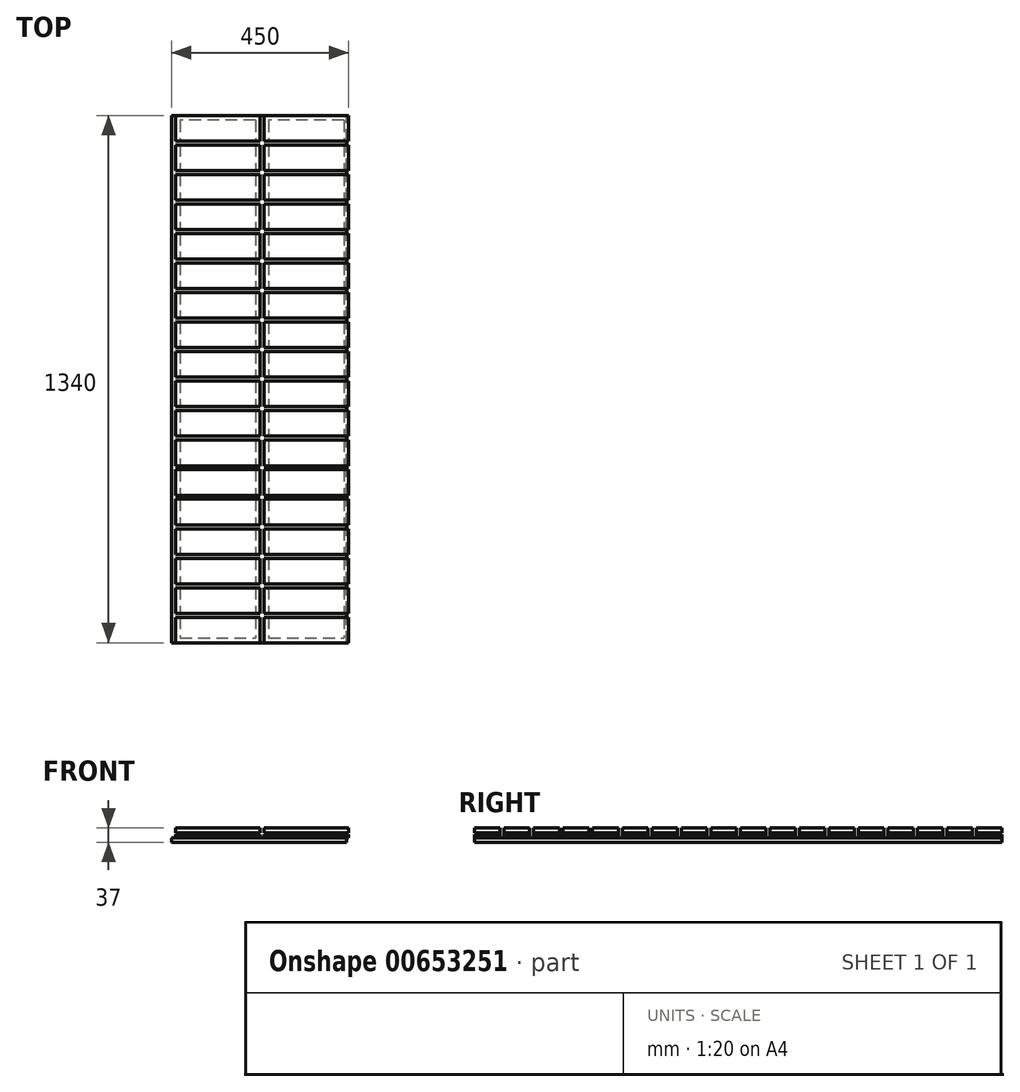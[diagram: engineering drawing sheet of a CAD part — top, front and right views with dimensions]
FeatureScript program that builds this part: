
annotation { "Feature Type Name" : "Feature", "Feature Type Description" : "" }
export const myFeature = defineFeature(function(context is Context, id is Id, definition is map)
    precondition{}
    {
        {
            var Q0;
            Q0=qCreatedBy(makeId("Top.planeOp"),FACE);
            var sketch = newSketch(context, id + "F0", { "sketchPlane" : qUnion([Q0])});
            skLineSegment(sketch, "E0", {"start": v(-211.36, 1125) * mm, "end": v(-211.36, 1190) * mm});
            skLineSegment(sketch, "E1", {"start": v(-211.36, 1190) * mm, "end": v(3.64, 1190) * mm});
            skLineSegment(sketch, "E2", {"start": v(3.64, 1190) * mm, "end": v(3.64, 1125) * mm});
            skLineSegment(sketch, "E3", {"start": v(3.64, 1125) * mm, "end": v(-211.36, 1125) * mm});
            skLineSegment(sketch, "E4", {"start": v(-211.36, 1200) * mm, "end": v(-211.36, 1265) * mm});
            skLineSegment(sketch, "E5", {"start": v(-211.36, 1265) * mm, "end": v(3.64, 1265) * mm});
            skLineSegment(sketch, "E6", {"start": v(3.64, 1265) * mm, "end": v(3.64, 1200) * mm});
            skLineSegment(sketch, "E7", {"start": v(3.64, 1200) * mm, "end": v(-211.36, 1200) * mm});
            skLineSegment(sketch, "E8", {"start": v(-211.36, 1275) * mm, "end": v(-211.36, 1340) * mm});
            skLineSegment(sketch, "E9", {"start": v(-211.36, 1340) * mm, "end": v(3.64, 1340) * mm});
            skLineSegment(sketch, "E10", {"start": v(3.64, 1340) * mm, "end": v(3.64, 1275) * mm});
            skLineSegment(sketch, "E11", {"start": v(3.64, 1275) * mm, "end": v(-211.36, 1275) * mm});
            skLineSegment(sketch, "E12", {"start": v(-436.36, 1125) * mm, "end": v(-436.36, 1190) * mm});
            skLineSegment(sketch, "E13", {"start": v(-436.36, 1190) * mm, "end": v(-221.36, 1190) * mm});
            skLineSegment(sketch, "E14", {"start": v(-221.36, 1190) * mm, "end": v(-221.36, 1125) * mm});
            skLineSegment(sketch, "E15", {"start": v(-221.36, 1125) * mm, "end": v(-436.36, 1125) * mm});
            skLineSegment(sketch, "E16", {"start": v(-436.36, 1200) * mm, "end": v(-436.36, 1265) * mm});
            skLineSegment(sketch, "E17", {"start": v(-436.36, 1265) * mm, "end": v(-221.36, 1265) * mm});
            skLineSegment(sketch, "E18", {"start": v(-221.36, 1265) * mm, "end": v(-221.36, 1200) * mm});
            skLineSegment(sketch, "E19", {"start": v(-221.36, 1200) * mm, "end": v(-436.36, 1200) * mm});
            skLineSegment(sketch, "E20", {"start": v(-436.36, 1275) * mm, "end": v(-436.36, 1340) * mm});
            skLineSegment(sketch, "E21", {"start": v(-436.36, 1340) * mm, "end": v(-221.36, 1340) * mm});
            skLineSegment(sketch, "E22", {"start": v(-221.36, 1340) * mm, "end": v(-221.36, 1275) * mm});
            skLineSegment(sketch, "E23", {"start": v(-221.36, 1275) * mm, "end": v(-436.36, 1275) * mm});
            skLineSegment(sketch, "E24", {"start": v(-211.36, 900) * mm, "end": v(-211.36, 965) * mm});
            skLineSegment(sketch, "E25", {"start": v(-211.36, 965) * mm, "end": v(3.64, 965) * mm});
            skLineSegment(sketch, "E26", {"start": v(3.64, 965) * mm, "end": v(3.64, 900) * mm});
            skLineSegment(sketch, "E27", {"start": v(3.64, 900) * mm, "end": v(-211.36, 900) * mm});
            skLineSegment(sketch, "E28", {"start": v(-211.36, 975) * mm, "end": v(-211.36, 1040) * mm});
            skLineSegment(sketch, "E29", {"start": v(-211.36, 1040) * mm, "end": v(3.64, 1040) * mm});
            skLineSegment(sketch, "E30", {"start": v(3.64, 1040) * mm, "end": v(3.64, 975) * mm});
            skLineSegment(sketch, "E31", {"start": v(3.64, 975) * mm, "end": v(-211.36, 975) * mm});
            skLineSegment(sketch, "E32", {"start": v(-211.36, 1050) * mm, "end": v(-211.36, 1115) * mm});
            skLineSegment(sketch, "E33", {"start": v(-211.36, 1115) * mm, "end": v(3.64, 1115) * mm});
            skLineSegment(sketch, "E34", {"start": v(3.64, 1115) * mm, "end": v(3.64, 1050) * mm});
            skLineSegment(sketch, "E35", {"start": v(3.64, 1050) * mm, "end": v(-211.36, 1050) * mm});
            skLineSegment(sketch, "E36", {"start": v(-436.36, 900) * mm, "end": v(-436.36, 965) * mm});
            skLineSegment(sketch, "E37", {"start": v(-436.36, 965) * mm, "end": v(-221.36, 965) * mm});
            skLineSegment(sketch, "E38", {"start": v(-221.36, 965) * mm, "end": v(-221.36, 900) * mm});
            skLineSegment(sketch, "E39", {"start": v(-221.36, 900) * mm, "end": v(-436.36, 900) * mm});
            skLineSegment(sketch, "E40", {"start": v(-436.36, 975) * mm, "end": v(-436.36, 1040) * mm});
            skLineSegment(sketch, "E41", {"start": v(-436.36, 1040) * mm, "end": v(-221.36, 1040) * mm});
            skLineSegment(sketch, "E42", {"start": v(-221.36, 1040) * mm, "end": v(-221.36, 975) * mm});
            skLineSegment(sketch, "E43", {"start": v(-221.36, 975) * mm, "end": v(-436.36, 975) * mm});
            skLineSegment(sketch, "E44", {"start": v(-436.36, 1050) * mm, "end": v(-436.36, 1115) * mm});
            skLineSegment(sketch, "E45", {"start": v(-436.36, 1115) * mm, "end": v(-221.36, 1115) * mm});
            skLineSegment(sketch, "E46", {"start": v(-221.36, 1115) * mm, "end": v(-221.36, 1050) * mm});
            skLineSegment(sketch, "E47", {"start": v(-221.36, 1050) * mm, "end": v(-436.36, 1050) * mm});
            skLineSegment(sketch, "E48", {"start": v(-211.36, 675) * mm, "end": v(-211.36, 740) * mm});
            skLineSegment(sketch, "E49", {"start": v(-211.36, 740) * mm, "end": v(3.64, 740) * mm});
            skLineSegment(sketch, "E50", {"start": v(3.64, 740) * mm, "end": v(3.64, 675) * mm});
            skLineSegment(sketch, "E51", {"start": v(3.64, 675) * mm, "end": v(-211.36, 675) * mm});
            skLineSegment(sketch, "E52", {"start": v(-211.36, 750) * mm, "end": v(-211.36, 815) * mm});
            skLineSegment(sketch, "E53", {"start": v(-211.36, 815) * mm, "end": v(3.64, 815) * mm});
            skLineSegment(sketch, "E54", {"start": v(3.64, 815) * mm, "end": v(3.64, 750) * mm});
            skLineSegment(sketch, "E55", {"start": v(3.64, 750) * mm, "end": v(-211.36, 750) * mm});
            skLineSegment(sketch, "E56", {"start": v(-211.36, 825) * mm, "end": v(-211.36, 890) * mm});
            skLineSegment(sketch, "E57", {"start": v(-211.36, 890) * mm, "end": v(3.64, 890) * mm});
            skLineSegment(sketch, "E58", {"start": v(3.64, 890) * mm, "end": v(3.64, 825) * mm});
            skLineSegment(sketch, "E59", {"start": v(3.64, 825) * mm, "end": v(-211.36, 825) * mm});
            skLineSegment(sketch, "E60", {"start": v(-436.36, 675) * mm, "end": v(-436.36, 740) * mm});
            skLineSegment(sketch, "E61", {"start": v(-436.36, 740) * mm, "end": v(-221.36, 740) * mm});
            skLineSegment(sketch, "E62", {"start": v(-221.36, 740) * mm, "end": v(-221.36, 675) * mm});
            skLineSegment(sketch, "E63", {"start": v(-221.36, 675) * mm, "end": v(-436.36, 675) * mm});
            skLineSegment(sketch, "E64", {"start": v(-436.36, 750) * mm, "end": v(-436.36, 815) * mm});
            skLineSegment(sketch, "E65", {"start": v(-436.36, 815) * mm, "end": v(-221.36, 815) * mm});
            skLineSegment(sketch, "E66", {"start": v(-221.36, 815) * mm, "end": v(-221.36, 750) * mm});
            skLineSegment(sketch, "E67", {"start": v(-221.36, 750) * mm, "end": v(-436.36, 750) * mm});
            skLineSegment(sketch, "E68", {"start": v(-436.36, 825) * mm, "end": v(-436.36, 890) * mm});
            skLineSegment(sketch, "E69", {"start": v(-436.36, 890) * mm, "end": v(-221.36, 890) * mm});
            skLineSegment(sketch, "E70", {"start": v(-221.36, 890) * mm, "end": v(-221.36, 825) * mm});
            skLineSegment(sketch, "E71", {"start": v(-221.36, 825) * mm, "end": v(-436.36, 825) * mm});
            skLineSegment(sketch, "E72", {"start": v(-211.36, 450) * mm, "end": v(-211.36, 515) * mm});
            skLineSegment(sketch, "E73", {"start": v(-211.36, 515) * mm, "end": v(3.64, 515) * mm});
            skLineSegment(sketch, "E74", {"start": v(3.64, 515) * mm, "end": v(3.64, 450) * mm});
            skLineSegment(sketch, "E75", {"start": v(3.64, 450) * mm, "end": v(-211.36, 450) * mm});
            skLineSegment(sketch, "E76", {"start": v(-211.36, 525) * mm, "end": v(-211.36, 590) * mm});
            skLineSegment(sketch, "E77", {"start": v(-211.36, 590) * mm, "end": v(3.64, 590) * mm});
            skLineSegment(sketch, "E78", {"start": v(3.64, 590) * mm, "end": v(3.64, 525) * mm});
            skLineSegment(sketch, "E79", {"start": v(3.64, 525) * mm, "end": v(-211.36, 525) * mm});
            skLineSegment(sketch, "E80", {"start": v(-211.36, 600) * mm, "end": v(-211.36, 665) * mm});
            skLineSegment(sketch, "E81", {"start": v(-211.36, 665) * mm, "end": v(3.64, 665) * mm});
            skLineSegment(sketch, "E82", {"start": v(3.64, 665) * mm, "end": v(3.64, 600) * mm});
            skLineSegment(sketch, "E83", {"start": v(3.64, 600) * mm, "end": v(-211.36, 600) * mm});
            skLineSegment(sketch, "E84", {"start": v(-436.36, 450) * mm, "end": v(-436.36, 515) * mm});
            skLineSegment(sketch, "E85", {"start": v(-436.36, 515) * mm, "end": v(-221.36, 515) * mm});
            skLineSegment(sketch, "E86", {"start": v(-221.36, 515) * mm, "end": v(-221.36, 450) * mm});
            skLineSegment(sketch, "E87", {"start": v(-221.36, 450) * mm, "end": v(-436.36, 450) * mm});
            skLineSegment(sketch, "E88", {"start": v(-436.36, 525) * mm, "end": v(-436.36, 590) * mm});
            skLineSegment(sketch, "E89", {"start": v(-436.36, 590) * mm, "end": v(-221.36, 590) * mm});
            skLineSegment(sketch, "E90", {"start": v(-221.36, 590) * mm, "end": v(-221.36, 525) * mm});
            skLineSegment(sketch, "E91", {"start": v(-221.36, 525) * mm, "end": v(-436.36, 525) * mm});
            skLineSegment(sketch, "E92", {"start": v(-436.36, 600) * mm, "end": v(-436.36, 665) * mm});
            skLineSegment(sketch, "E93", {"start": v(-436.36, 665) * mm, "end": v(-221.36, 665) * mm});
            skLineSegment(sketch, "E94", {"start": v(-221.36, 665) * mm, "end": v(-221.36, 600) * mm});
            skLineSegment(sketch, "E95", {"start": v(-221.36, 600) * mm, "end": v(-436.36, 600) * mm});
            skLineSegment(sketch, "E96", {"start": v(-211.36, 225) * mm, "end": v(-211.36, 290) * mm});
            skLineSegment(sketch, "E97", {"start": v(-211.36, 290) * mm, "end": v(3.64, 290) * mm});
            skLineSegment(sketch, "E98", {"start": v(3.64, 290) * mm, "end": v(3.64, 225) * mm});
            skLineSegment(sketch, "E99", {"start": v(3.64, 225) * mm, "end": v(-211.36, 225) * mm});
            skLineSegment(sketch, "E100", {"start": v(-211.36, 300) * mm, "end": v(-211.36, 365) * mm});
            skLineSegment(sketch, "E101", {"start": v(-211.36, 365) * mm, "end": v(3.64, 365) * mm});
            skLineSegment(sketch, "E102", {"start": v(3.64, 365) * mm, "end": v(3.64, 300) * mm});
            skLineSegment(sketch, "E103", {"start": v(3.64, 300) * mm, "end": v(-211.36, 300) * mm});
            skLineSegment(sketch, "E104", {"start": v(-211.36, 375) * mm, "end": v(-211.36, 440) * mm});
            skLineSegment(sketch, "E105", {"start": v(-211.36, 440) * mm, "end": v(3.64, 440) * mm});
            skLineSegment(sketch, "E106", {"start": v(3.64, 440) * mm, "end": v(3.64, 375) * mm});
            skLineSegment(sketch, "E107", {"start": v(3.64, 375) * mm, "end": v(-211.36, 375) * mm});
            skLineSegment(sketch, "E108", {"start": v(-436.36, 225) * mm, "end": v(-436.36, 290) * mm});
            skLineSegment(sketch, "E109", {"start": v(-436.36, 290) * mm, "end": v(-221.36, 290) * mm});
            skLineSegment(sketch, "E110", {"start": v(-221.36, 290) * mm, "end": v(-221.36, 225) * mm});
            skLineSegment(sketch, "E111", {"start": v(-221.36, 225) * mm, "end": v(-436.36, 225) * mm});
            skLineSegment(sketch, "E112", {"start": v(-436.36, 300) * mm, "end": v(-436.36, 365) * mm});
            skLineSegment(sketch, "E113", {"start": v(-436.36, 365) * mm, "end": v(-221.36, 365) * mm});
            skLineSegment(sketch, "E114", {"start": v(-221.36, 365) * mm, "end": v(-221.36, 300) * mm});
            skLineSegment(sketch, "E115", {"start": v(-221.36, 300) * mm, "end": v(-436.36, 300) * mm});
            skLineSegment(sketch, "E116", {"start": v(-436.36, 375) * mm, "end": v(-436.36, 440) * mm});
            skLineSegment(sketch, "E117", {"start": v(-436.36, 440) * mm, "end": v(-221.36, 440) * mm});
            skLineSegment(sketch, "E118", {"start": v(-221.36, 440) * mm, "end": v(-221.36, 375) * mm});
            skLineSegment(sketch, "E119", {"start": v(-221.36, 375) * mm, "end": v(-436.36, 375) * mm});
            skLineSegment(sketch, "E120", {"start": v(-211.36, 0) * mm, "end": v(-211.36, 65) * mm});
            skLineSegment(sketch, "E121", {"start": v(-211.36, 65) * mm, "end": v(3.64, 65) * mm});
            skLineSegment(sketch, "E122", {"start": v(3.64, 65) * mm, "end": v(3.64, 0) * mm});
            skLineSegment(sketch, "E123", {"start": v(3.64, 0) * mm, "end": v(-211.36, 0) * mm});
            skLineSegment(sketch, "E124", {"start": v(-211.36, 75) * mm, "end": v(-211.36, 140) * mm});
            skLineSegment(sketch, "E125", {"start": v(-211.36, 140) * mm, "end": v(3.64, 140) * mm});
            skLineSegment(sketch, "E126", {"start": v(3.64, 140) * mm, "end": v(3.64, 75) * mm});
            skLineSegment(sketch, "E127", {"start": v(3.64, 75) * mm, "end": v(-211.36, 75) * mm});
            skLineSegment(sketch, "E128", {"start": v(-211.36, 150) * mm, "end": v(-211.36, 215) * mm});
            skLineSegment(sketch, "E129", {"start": v(-211.36, 215) * mm, "end": v(3.64, 215) * mm});
            skLineSegment(sketch, "E130", {"start": v(3.64, 215) * mm, "end": v(3.64, 150) * mm});
            skLineSegment(sketch, "E131", {"start": v(3.64, 150) * mm, "end": v(-211.36, 150) * mm});
            skLineSegment(sketch, "E132", {"start": v(-436.36, 0) * mm, "end": v(-436.36, 65) * mm});
            skLineSegment(sketch, "E133", {"start": v(-436.36, 65) * mm, "end": v(-221.36, 65) * mm});
            skLineSegment(sketch, "E134", {"start": v(-221.36, 65) * mm, "end": v(-221.36, 0) * mm});
            skLineSegment(sketch, "E135", {"start": v(-221.36, 0) * mm, "end": v(-436.36, 0) * mm});
            skLineSegment(sketch, "E136", {"start": v(-436.36, 75) * mm, "end": v(-436.36, 140) * mm});
            skLineSegment(sketch, "E137", {"start": v(-436.36, 140) * mm, "end": v(-221.36, 140) * mm});
            skLineSegment(sketch, "E138", {"start": v(-221.36, 140) * mm, "end": v(-221.36, 75) * mm});
            skLineSegment(sketch, "E139", {"start": v(-221.36, 75) * mm, "end": v(-436.36, 75) * mm});
            skLineSegment(sketch, "E140", {"start": v(-436.36, 150) * mm, "end": v(-436.36, 215) * mm});
            skLineSegment(sketch, "E141", {"start": v(-436.36, 215) * mm, "end": v(-221.36, 215) * mm});
            skLineSegment(sketch, "E142", {"start": v(-221.36, 215) * mm, "end": v(-221.36, 150) * mm});
            skLineSegment(sketch, "E143", {"start": v(-221.36, 150) * mm, "end": v(-436.36, 150) * mm});
            skSolve(sketch);
        }
        {
            var Q0;
            Q0 = qSketchRegion(id + "F0", true);
            extrude(context, id + "F1", {"entities" : qUnion([Q0]), "depth" : 25 * mm, "offsetDistance" : 25 * mm});
        }
        {
            var Q0;
            Q0=makeQuery(id+"F1.opExtrude","SWEPT_FACE",FACE,{"disambiguationData":[OSD([sQuery(id+"F0.wireOp",EDGE,"E123")])]});
            var sketch = newSketch(context, id + "F2", { "sketchPlane" : qUnion([Q0])});
            skLineSegment(sketch, "E144.bottom", {"start": v(-211.36, 8) * mm, "end": v(-199.36, 8) * mm});
            skLineSegment(sketch, "E144.top", {"start": v(-211.36, 12) * mm, "end": v(-199.36, 12) * mm});
            skLineSegment(sketch, "E144.left", {"start": v(-211.36, 8) * mm, "end": v(-211.36, 12) * mm});
            skLineSegment(sketch, "E144.right", {"start": v(-199.36, 8) * mm, "end": v(-199.36, 12) * mm});
            skLineSegment(sketch, "E145.MirrorCS", {"start": v(-8.36, 8) * mm, "end": v(-8.36, 12) * mm});
            skLineSegment(sketch, "E146.MirrorCS", {"start": v(3.64, 12) * mm, "end": v(-8.36, 12) * mm});
            skLineSegment(sketch, "E147.MirrorCS", {"start": v(3.64, 8) * mm, "end": v(-8.36, 8) * mm});
            skLineSegment(sketch, "E148.MirrorCS", {"start": v(3.64, 8) * mm, "end": v(3.64, 12) * mm});
            skSolve(sketch);
        }
        {
            var Q0;
            Q0=makeQuery(id+"F1.opExtrude","SWEPT_FACE",FACE,{"disambiguationData":[OSD([sQuery(id+"F0.wireOp",EDGE,"E135")])]});
            var sketch = newSketch(context, id + "F3", { "sketchPlane" : qUnion([Q0])});
            skLineSegment(sketch, "E149.bottom", {"start": v(-436.36, 8) * mm, "end": v(-424.36, 8) * mm});
            skLineSegment(sketch, "E149.top", {"start": v(-436.36, 12) * mm, "end": v(-424.36, 12) * mm});
            skLineSegment(sketch, "E149.left", {"start": v(-436.36, 8) * mm, "end": v(-436.36, 12) * mm});
            skLineSegment(sketch, "E149.right", {"start": v(-424.36, 8) * mm, "end": v(-424.36, 12) * mm});
            skLineSegment(sketch, "E150.MirrorCS", {"start": v(-233.36, 8) * mm, "end": v(-233.36, 12) * mm});
            skLineSegment(sketch, "E151.MirrorCS", {"start": v(-221.36, 12) * mm, "end": v(-233.36, 12) * mm});
            skLineSegment(sketch, "E152.MirrorCS", {"start": v(-221.36, 8) * mm, "end": v(-233.36, 8) * mm});
            skLineSegment(sketch, "E153.MirrorCS", {"start": v(-221.36, 8) * mm, "end": v(-221.36, 12) * mm});
            skSolve(sketch);
        }
        {
            var Q0;
            Q0=makeQuery(id+"F2.imprint","IMPRINT",FACE,{"disambiguationData":[TD([[makeQuery(id+"F2.imprint","IMPRINT",EDGE,{"derivedFrom":sQuery(id+"F2.wireOp",EDGE,"E145.MirrorCS")}),-1.0]])]});
            var Q1;
            Q1=makeQuery(id+"F2.imprint","IMPRINT",FACE,{"disambiguationData":[TD([[makeQuery(id+"F2.imprint","IMPRINT",EDGE,{"derivedFrom":sQuery(id+"F2.wireOp",EDGE,"E144.bottom")}),1.0]])]});
            var Q2;
            Q2=makeQuery(id+"F3.imprint","IMPRINT",FACE,{"disambiguationData":[TD([[makeQuery(id+"F3.imprint","IMPRINT",EDGE,{"derivedFrom":sQuery(id+"F3.wireOp",EDGE,"E150.MirrorCS")}),-1.0]])]});
            var Q3;
            Q3=makeQuery(id+"F3.imprint","IMPRINT",FACE,{"disambiguationData":[TD([[makeQuery(id+"F3.imprint","IMPRINT",EDGE,{"derivedFrom":sQuery(id+"F3.wireOp",EDGE,"E149.bottom")}),1.0]])]});
            extrude(context, id + "F4", {"entities" : qUnion([Q0, Q1, Q2, Q3]), "operationType" : NewBodyOperationType.REMOVE, "endBound" : BoundingType.THROUGH_ALL, "oppositeDirection" : true, "depth" : 25 * mm, "offsetDistance" : 25 * mm});
        }
        {
            var Q0;
            Q0=qCreatedBy(makeId("Top.planeOp"),FACE);
            var sketch = newSketch(context, id + "F5", { "sketchPlane" : qUnion([Q0])});
            skLineSegment(sketch, "E154.bottom", {"start": v(-1.36, 0) * mm, "end": v(-446.36, 0) * mm});
            skLineSegment(sketch, "E154.top", {"start": v(-1.36, 1340) * mm, "end": v(-446.36, 1340) * mm});
            skLineSegment(sketch, "E154.left", {"start": v(-1.36, 0) * mm, "end": v(-1.36, 1340) * mm});
            skLineSegment(sketch, "E154.right", {"start": v(-446.36, 0) * mm, "end": v(-446.36, 1340) * mm});
            skSolve(sketch);
        }
        {
            var Q0;
            Q0 = qSketchRegion(id + "F5", true);
            extrude(context, id + "F6", {"entities" : qUnion([Q0]), "oppositeDirection" : true, "depth" : 12 * mm, "offsetDistance" : 25 * mm});
        }
        {
            var Q0;
            Q0=makeQuery(id+"F1.opExtrude","SWEPT_FACE",FACE,{"disambiguationData":[OSD([sQuery(id+"F0.wireOp",EDGE,"E123")])]});
            var sketch = newSketch(context, id + "F7", { "sketchPlane" : qUnion([Q0])});
            skLineSegment(sketch, "E155.bottom", {"start": v(-199.36, 8) * mm, "end": v(-8.36, 8) * mm});
            skLineSegment(sketch, "E155.top", {"start": v(-199.36, 12) * mm, "end": v(-8.36, 12) * mm});
            skLineSegment(sketch, "E155.left", {"start": v(-199.36, 8) * mm, "end": v(-199.36, 12) * mm});
            skLineSegment(sketch, "E155.right", {"start": v(-8.36, 8) * mm, "end": v(-8.36, 12) * mm});
            skSolve(sketch);
        }
        {
            var Q0;
            Q0=makeQuery(id+"F7.imprint","IMPRINT",FACE,{"disambiguationData":[TD([[makeQuery(id+"F7.imprint","IMPRINT",EDGE,{"derivedFrom":sQuery(id+"F7.wireOp",EDGE,"E155.bottom")}),1.0]])]});
            extrude(context, id + "F8", {"entities" : qUnion([Q0]), "operationType" : NewBodyOperationType.REMOVE, "oppositeDirection" : true, "depth" : 12 * mm, "offsetDistance" : 25 * mm});
        }
        {
            var Q0;
            Q0=makeQuery(id+"F1.opExtrude","SWEPT_FACE",FACE,{"disambiguationData":[OSD([sQuery(id+"F0.wireOp",EDGE,"E135")])]});
            var sketch = newSketch(context, id + "F9", { "sketchPlane" : qUnion([Q0])});
            skLineSegment(sketch, "E156.bottom", {"start": v(-424.36, 8) * mm, "end": v(-233.36, 8) * mm});
            skLineSegment(sketch, "E156.top", {"start": v(-424.36, 12) * mm, "end": v(-233.36, 12) * mm});
            skLineSegment(sketch, "E156.left", {"start": v(-424.36, 8) * mm, "end": v(-424.36, 12) * mm});
            skLineSegment(sketch, "E156.right", {"start": v(-233.36, 8) * mm, "end": v(-233.36, 12) * mm});
            skSolve(sketch);
        }
        {
            var Q0;
            Q0=makeQuery(id+"F9.imprint","IMPRINT",FACE,{"disambiguationData":[TD([[makeQuery(id+"F9.imprint","IMPRINT",EDGE,{"derivedFrom":sQuery(id+"F9.wireOp",EDGE,"E156.bottom")}),1.0]])]});
            extrude(context, id + "F10", {"entities" : qUnion([Q0]), "operationType" : NewBodyOperationType.REMOVE, "oppositeDirection" : true, "depth" : 12 * mm, "offsetDistance" : 25 * mm});
        }
        {
            var Q0;
            Q0=makeQuery(id+"F1.opExtrude","SWEPT_FACE",FACE,{"disambiguationData":[OSD([sQuery(id+"F0.wireOp",EDGE,"E9")])]});
            var sketch = newSketch(context, id + "F11", { "sketchPlane" : qUnion([Q0])});
            skLineSegment(sketch, "E157.bottom", {"start": v(8.36, 8) * mm, "end": v(199.36, 8) * mm});
            skLineSegment(sketch, "E157.top", {"start": v(8.36, 12) * mm, "end": v(199.36, 12) * mm});
            skLineSegment(sketch, "E157.left", {"start": v(8.36, 8) * mm, "end": v(8.36, 12) * mm});
            skLineSegment(sketch, "E157.right", {"start": v(199.36, 8) * mm, "end": v(199.36, 12) * mm});
            skSolve(sketch);
        }
        {
            var Q0;
            Q0=makeQuery(id+"F11.imprint","IMPRINT",FACE,{"disambiguationData":[TD([[makeQuery(id+"F11.imprint","IMPRINT",EDGE,{"derivedFrom":sQuery(id+"F11.wireOp",EDGE,"E157.bottom")}),1.0]])]});
            extrude(context, id + "F12", {"entities" : qUnion([Q0]), "operationType" : NewBodyOperationType.REMOVE, "oppositeDirection" : true, "depth" : 12 * mm, "offsetDistance" : 25 * mm});
        }
        {
            var Q0;
            Q0=makeQuery(id+"F1.opExtrude","SWEPT_FACE",FACE,{"disambiguationData":[OSD([sQuery(id+"F0.wireOp",EDGE,"E21")])]});
            var sketch = newSketch(context, id + "F13", { "sketchPlane" : qUnion([Q0])});
            skLineSegment(sketch, "E158.bottom", {"start": v(233.36, 8) * mm, "end": v(424.36, 8) * mm});
            skLineSegment(sketch, "E158.top", {"start": v(233.36, 12) * mm, "end": v(424.36, 12) * mm});
            skLineSegment(sketch, "E158.left", {"start": v(233.36, 8) * mm, "end": v(233.36, 12) * mm});
            skLineSegment(sketch, "E158.right", {"start": v(424.36, 8) * mm, "end": v(424.36, 12) * mm});
            skSolve(sketch);
        }
        {
            var Q0;
            Q0=makeQuery(id+"F13.imprint","IMPRINT",FACE,{"disambiguationData":[TD([[makeQuery(id+"F13.imprint","IMPRINT",EDGE,{"derivedFrom":sQuery(id+"F13.wireOp",EDGE,"E158.bottom")}),1.0]])]});
            extrude(context, id + "F14", {"entities" : qUnion([Q0]), "operationType" : NewBodyOperationType.REMOVE, "oppositeDirection" : true, "depth" : 12 * mm, "offsetDistance" : 25 * mm});
        }
    });
